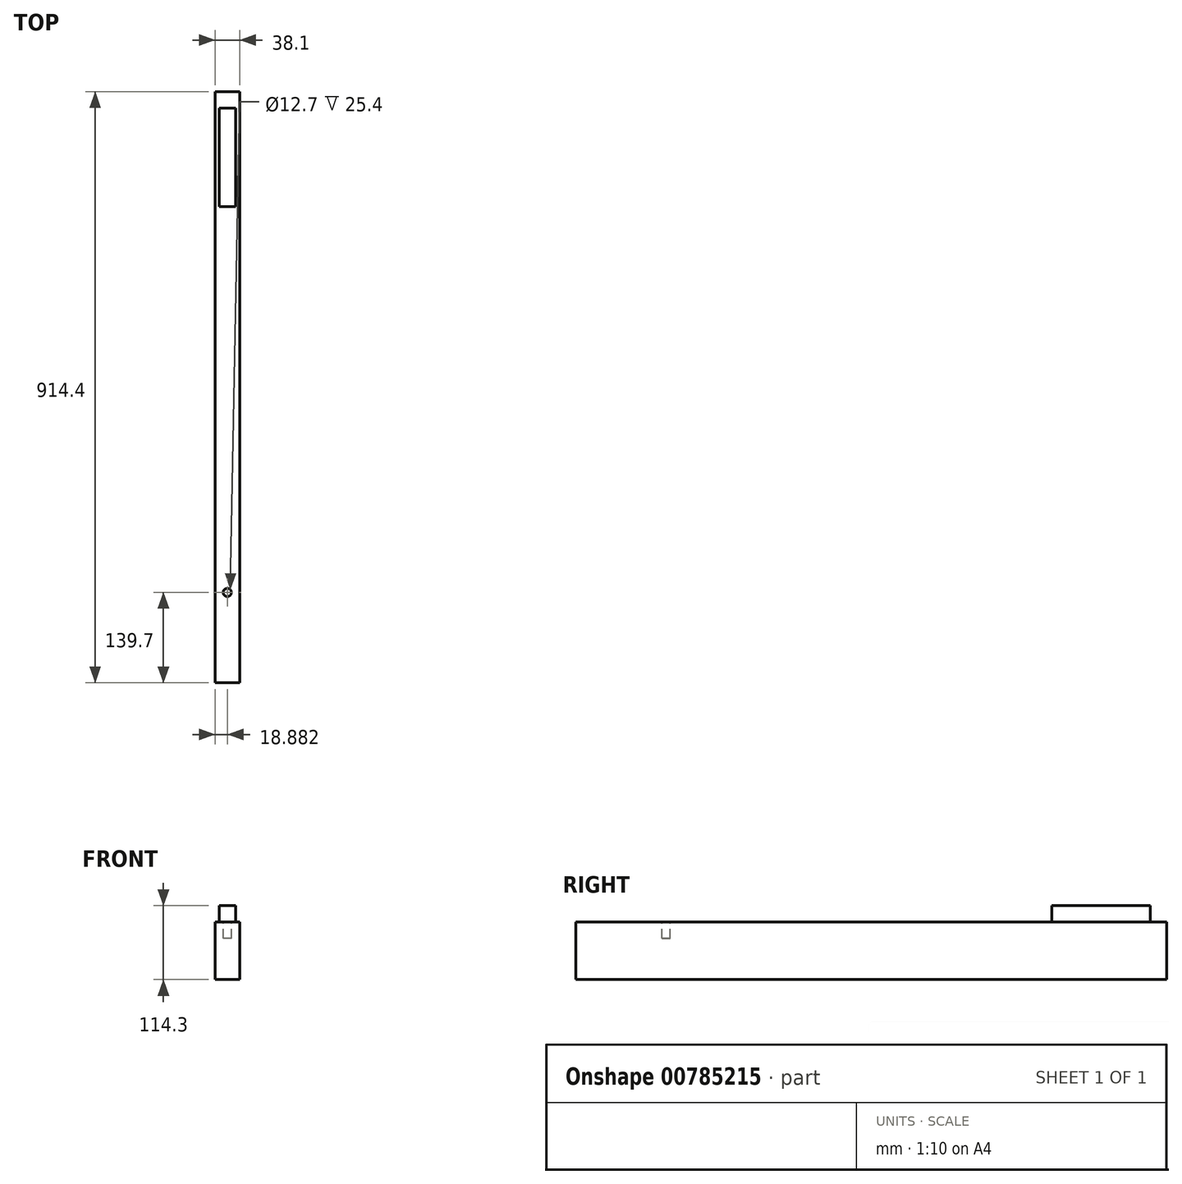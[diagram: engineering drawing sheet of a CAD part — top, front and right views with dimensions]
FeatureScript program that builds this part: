
annotation { "Feature Type Name" : "Feature", "Feature Type Description" : "" }
export const myFeature = defineFeature(function(context is Context, id is Id, definition is map)
    precondition{}
    {
        {
            var Q0;
            Q0=qCreatedBy(makeId("Right.planeOp"),FACE);
            var sketch = newSketch(context, id + "F0", { "sketchPlane" : qUnion([Q0])});
            skLineSegment(sketch, "E0.bottom", {"start": v(-457.2, 44.45) * mm, "end": v(457.2, 44.45) * mm});
            skLineSegment(sketch, "E0.top", {"start": v(-457.2, -44.45) * mm, "end": v(457.2, -44.45) * mm});
            skLineSegment(sketch, "E0.left", {"start": v(-457.2, 44.45) * mm, "end": v(-457.2, -44.45) * mm});
            skLineSegment(sketch, "E0.right", {"start": v(457.2, 44.45) * mm, "end": v(457.2, -44.45) * mm});
            skSolve(sketch);
        }
        {
            var Q0;
            Q0=makeQuery(id+"F0.imprint","IMPRINT",FACE,{"disambiguationData":[TD([[makeQuery(id+"F0.imprint","IMPRINT",EDGE,{"derivedFrom":sQuery(id+"F0.wireOp",EDGE,"E0.bottom")}),-1.0]])]});
            extrude(context, id + "F1", {"entities" : qUnion([Q0]), "depth" : 38.1 * mm, "offsetDistance" : 25.4 * mm});
        }
        {
            var Q0;
            Q0=makeQuery(id+"F1.opExtrude","SWEPT_FACE",FACE,{"disambiguationData":[OSD([sQuery(id+"F0.wireOp",EDGE,"E0.bottom")])]});
            var sketch = newSketch(context, id + "F2", { "sketchPlane" : qUnion([Q0])});
            skCircle(sketch, "E1", {"center": v(18.88, -317.5) * mm, "radius": 6.35 * mm});
            skSolve(sketch);
        }
        {
            var Q0;
            Q0=makeQuery(id+"F2.imprint","IMPRINT",FACE,{"disambiguationData":[TD([[makeQuery(id+"F2.imprint","IMPRINT",EDGE,{"derivedFrom":sQuery(id+"F2.wireOp",EDGE,"E1")}),1.0]])]});
            extrude(context, id + "F3", {"entities" : qUnion([Q0]), "operationType" : NewBodyOperationType.REMOVE, "oppositeDirection" : true, "depth" : 25.4 * mm, "offsetDistance" : 25.4 * mm});
        }
        {
            var Q0;
            Q0=makeQuery(id+"F1.opExtrude","SWEPT_FACE",FACE,{"disambiguationData":[OSD([sQuery(id+"F0.wireOp",EDGE,"E0.bottom")])]});
            var sketch = newSketch(context, id + "F4", { "sketchPlane" : qUnion([Q0])});
            skLineSegment(sketch, "E2.bottom", {"start": v(6.35, 431.8) * mm, "end": v(31.75, 431.8) * mm});
            skLineSegment(sketch, "E2.top", {"start": v(6.35, 279.4) * mm, "end": v(31.75, 279.4) * mm});
            skLineSegment(sketch, "E2.left", {"start": v(6.35, 431.8) * mm, "end": v(6.35, 279.4) * mm});
            skLineSegment(sketch, "E2.right", {"start": v(31.75, 431.8) * mm, "end": v(31.75, 279.4) * mm});
            skSolve(sketch);
        }
        {
            var Q0;
            Q0=makeQuery(id+"F4.imprint","IMPRINT",FACE,{"disambiguationData":[TD([[makeQuery(id+"F4.imprint","IMPRINT",EDGE,{"derivedFrom":sQuery(id+"F4.wireOp",EDGE,"E2.bottom")}),-1.0]])]});
            extrude(context, id + "F5", {"entities" : qUnion([Q0]), "operationType" : NewBodyOperationType.ADD, "depth" : 25.4 * mm, "offsetDistance" : 25.4 * mm});
        }
    });
